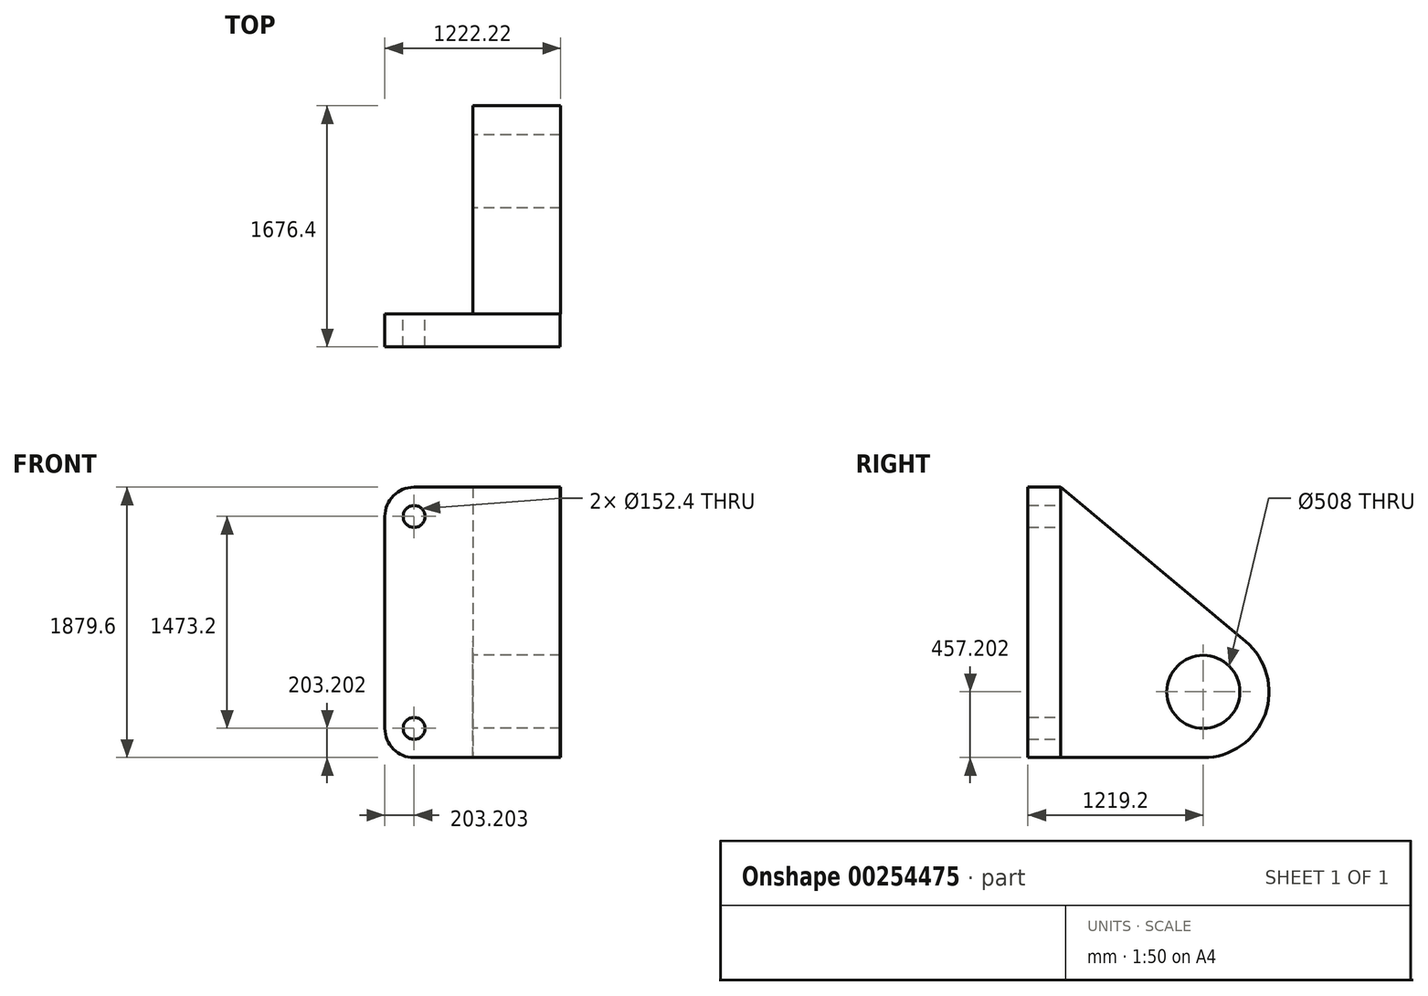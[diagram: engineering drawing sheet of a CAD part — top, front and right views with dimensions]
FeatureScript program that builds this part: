
annotation { "Feature Type Name" : "Feature", "Feature Type Description" : "" }
export const myFeature = defineFeature(function(context is Context, id is Id, definition is map)
    precondition{}
    {
        {
            var Q0;
            Q0=qCreatedBy(makeId("Front.planeOp"),FACE);
            var sketch = newSketch(context, id + "F0", { "sketchPlane" : qUnion([Q0])});
            skLineSegment(sketch, "E0.bottom", {"start": v(606.58, 1056.12) * mm, "end": v(-409.42, 1056.12) * mm});
            skLineSegment(sketch, "E0.top", {"start": v(606.58, -823.48) * mm, "end": v(-409.42, -823.48) * mm});
            skLineSegment(sketch, "E0.left", {"start": v(606.58, 1056.12) * mm, "end": v(606.58, -823.48) * mm});
            skLineSegment(sketch, "E0.right", {"start": v(-612.62, 852.92) * mm, "end": v(-612.62, -620.28) * mm});
            skPoint(sketch, "E1.visualSharp", {"position": v(-612.62, 1056.12) * mm});
            skArc(sketch, "E1.filletArc", {"start": v(-409.42, 1056.12) * mm, "mid": v(-553.1, 996.6) * mm, "end": v(-612.62, 852.92) * mm});
            skPoint(sketch, "E2.visualSharp", {"position": v(-612.62, -823.48) * mm});
            skArc(sketch, "E2.filletArc", {"start": v(-612.62, -620.28) * mm, "mid": v(-553.1, -763.96) * mm, "end": v(-409.42, -823.48) * mm});
            skCircle(sketch, "E3", {"center": v(-409.42, 852.92) * mm, "radius": 76.2 * mm});
            skCircle(sketch, "E4", {"center": v(-409.42, -620.28) * mm, "radius": 76.2 * mm});
            skSolve(sketch);
        }
        {
            var Q0;
            Q0 = qSketchRegion(id + "F0", true);
            extrude(context, id + "F1", {"entities" : qUnion([Q0]), "depth" : 203.2 * mm});
        }
        {
            var Q0;
            Q0=makeQuery(id+"F1.opExtrude","CAP_FACE",FACE,{"disambiguationData":[OSD([sQuery(id+"F0.wireOp",EDGE,"E0.bottom"),sQuery(id+"F0.wireOp",EDGE,"E0.top"),sQuery(id+"F0.wireOp",EDGE,"E0.left"),sQuery(id+"F0.wireOp",EDGE,"E0.right"),sQuery(id+"F0.wireOp",EDGE,"E1.filletArc"),sQuery(id+"F0.wireOp",EDGE,"E2.filletArc"),sQuery(id+"F0.wireOp",EDGE,"E3"),sQuery(id+"F0.wireOp",EDGE,"E4")])],"isStart":true});
            extrude(context, id + "F2", {"entities" : qUnion([Q0]), "operationType" : NewBodyOperationType.ADD, "depth" : 25.4 * mm});
        }
        {
            var Q0;
            Q0=makeQuery(id+"F2.opExtrude","CAP_FACE",FACE,{"disambiguationData":[OSD([sQuery(id+"F0.wireOp",EDGE,"E0.bottom"),sQuery(id+"F0.wireOp",EDGE,"E0.top"),sQuery(id+"F0.wireOp",EDGE,"E0.left"),sQuery(id+"F0.wireOp",EDGE,"E0.right"),sQuery(id+"F0.wireOp",EDGE,"E1.filletArc"),sQuery(id+"F0.wireOp",EDGE,"E2.filletArc"),sQuery(id+"F0.wireOp",EDGE,"E3"),sQuery(id+"F0.wireOp",EDGE,"E4")])],"isStart":false});
            var sketch = newSketch(context, id + "F3", { "sketchPlane" : qUnion([Q0])});
            skLineSegment(sketch, "E5", {"start": v(-606.58, -823.48) * mm, "end": v(3.02, -823.48) * mm});
            skLineSegment(sketch, "E6", {"start": v(3.02, -823.48) * mm, "end": v(3.02, 1056.12) * mm});
            skLineSegment(sketch, "E7", {"start": v(3.02, 1056.12) * mm, "end": v(-606.58, 1056.12) * mm});
            skLineSegment(sketch, "E8", {"start": v(-606.58, 1056.12) * mm, "end": v(-606.58, -823.48) * mm});
            skSolve(sketch);
        }
        {
            var Q0;
            Q0=qCreatedBy(makeId("Right.planeOp"),FACE);
            var sketch = newSketch(context, id + "F4", { "sketchPlane" : qUnion([Q0])});
            skArc(sketch, "E9", {"start": v(1016, -823.48) * mm, "mid": v(1445.83, -522.1) * mm, "end": v(1308.98, -15.28) * mm});
            skLineSegment(sketch, "E10", {"start": v(25.4, -823.48) * mm, "end": v(1016, -823.48) * mm});
            skLineSegment(sketch, "E11", {"start": v(25.4, 1056.12) * mm, "end": v(1308.98, -15.28) * mm});
            skLineSegment(sketch, "E12", {"start": v(25.4, 1056.12) * mm, "end": v(25.4, -823.48) * mm});
            skSolve(sketch);
        }
        {
            var Q0;
            Q0=makeQuery(id+"F4.imprint","IMPRINT",FACE,{"disambiguationData":[TD([[makeQuery(id+"F4.imprint","IMPRINT",EDGE,{"derivedFrom":sQuery(id+"F4.wireOp",EDGE,"E9")}),1.0]])]});
            extrude(context, id + "F5", {"entities" : qUnion([Q0]), "operationType" : NewBodyOperationType.ADD, "depth" : 609.6 * mm});
        }
        {
            var Q0;
            Q0=makeQuery(id+"F4.imprint","IMPRINT",FACE,{"disambiguationData":[TD([[makeQuery(id+"F4.imprint","IMPRINT",EDGE,{"derivedFrom":sQuery(id+"F4.wireOp",EDGE,"E9")}),1.0]])]});
            var sketch = newSketch(context, id + "F6", { "sketchPlane" : qUnion([Q0])});
            skCircle(sketch, "E13", {"center": v(1016, -366.28) * mm, "radius": 254 * mm});
            skSolve(sketch);
        }
        {
            var Q0;
            Q0=makeQuery(id+"F6.imprint","IMPRINT",FACE,{"disambiguationData":[TD([[makeQuery(id+"F6.imprint","IMPRINT",EDGE,{"derivedFrom":sQuery(id+"F6.wireOp",EDGE,"E13")}),1.0]])]});
            extrude(context, id + "F7", {"entities" : qUnion([Q0]), "operationType" : NewBodyOperationType.REMOVE, "depth" : 1488.44 * mm});
        }
    });
